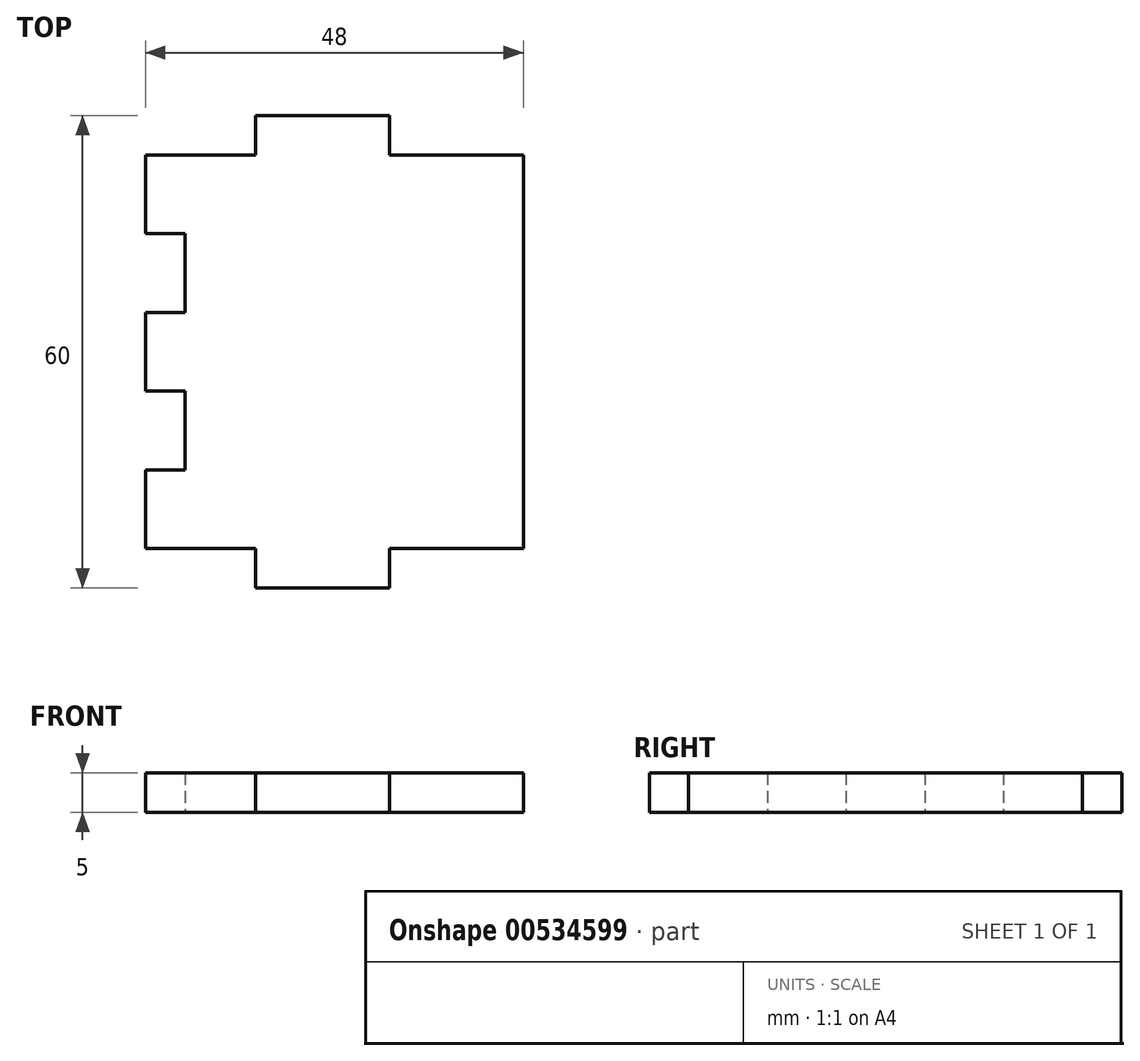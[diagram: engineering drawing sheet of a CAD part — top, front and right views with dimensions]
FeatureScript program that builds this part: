
annotation { "Feature Type Name" : "Feature", "Feature Type Description" : "" }
export const myFeature = defineFeature(function(context is Context, id is Id, definition is map)
    precondition{}
    {
        {
            var Q0;
            Q0=qCreatedBy(makeId("Top.planeOp"),FACE);
            var sketch = newSketch(context, id + "F0", { "sketchPlane" : qUnion([Q0])});
            skLineSegment(sketch, "E0.bottom", {"start": v(21.5, 25) * mm, "end": v(4.5, 25) * mm});
            skLineSegment(sketch, "E0.top", {"start": v(21.5, -25) * mm, "end": v(4.5, -25) * mm});
            skLineSegment(sketch, "E0.left", {"start": v(21.5, 25) * mm, "end": v(21.5, -25) * mm});
            skLineSegment(sketch, "E0.right", {"start": v(-21.5, 15) * mm, "end": v(-21.5, 5) * mm});
            skPoint(sketch, "E0.middle", {"position": v(0, 0) * mm});
            skLineSegment(sketch, "E1", {"start": v(21.5, -25) * mm, "end": v(21.5, -30) * mm, "construction": true});
            skLineSegment(sketch, "E2", {"start": v(21.5, -30) * mm, "end": v(-26.5, -30) * mm, "construction": true});
            skLineSegment(sketch, "E3", {"start": v(-26.5, -30) * mm, "end": v(-26.5, 30) * mm, "construction": true});
            skLineSegment(sketch, "E4", {"start": v(-26.5, 30) * mm, "end": v(21.5, 30) * mm, "construction": true});
            skLineSegment(sketch, "E5", {"start": v(21.5, 30) * mm, "end": v(21.5, 25) * mm, "construction": true});
            skLineSegment(sketch, "E6.top", {"start": v(4.5, 30) * mm, "end": v(-12.5, 30) * mm});
            skLineSegment(sketch, "E6.left", {"start": v(4.5, 25) * mm, "end": v(4.5, 30) * mm});
            skLineSegment(sketch, "E6.right", {"start": v(-12.5, 25) * mm, "end": v(-12.5, 30) * mm});
            skLineSegment(sketch, "E7.top", {"start": v(4.5, -30) * mm, "end": v(-12.5, -30) * mm});
            skLineSegment(sketch, "E7.left", {"start": v(4.5, -25) * mm, "end": v(4.5, -30) * mm});
            skLineSegment(sketch, "E7.right", {"start": v(-12.5, -25) * mm, "end": v(-12.5, -30) * mm});
            skLineSegment(sketch, "E8.trimOffspring", {"start": v(-12.5, 25) * mm, "end": v(-21.5, 25) * mm});
            skLineSegment(sketch, "E9.trimOffspring", {"start": v(-12.5, -25) * mm, "end": v(-21.5, -25) * mm});
            skLineSegment(sketch, "E10.bottom", {"start": v(-21.5, 25) * mm, "end": v(-26.5, 25) * mm});
            skLineSegment(sketch, "E10.top", {"start": v(-21.5, 15) * mm, "end": v(-26.5, 15) * mm});
            skLineSegment(sketch, "E10.right", {"start": v(-26.5, 25) * mm, "end": v(-26.5, 15) * mm});
            skLineSegment(sketch, "E11.bottom", {"start": v(-21.5, 5) * mm, "end": v(-26.5, 5) * mm});
            skLineSegment(sketch, "E11.top", {"start": v(-21.5, -5) * mm, "end": v(-26.5, -5) * mm});
            skLineSegment(sketch, "E11.right", {"start": v(-26.5, 5) * mm, "end": v(-26.5, -5) * mm});
            skLineSegment(sketch, "E12.bottom", {"start": v(-21.5, -25) * mm, "end": v(-26.5, -25) * mm});
            skLineSegment(sketch, "E12.top", {"start": v(-21.5, -15) * mm, "end": v(-26.5, -15) * mm});
            skLineSegment(sketch, "E12.right", {"start": v(-26.5, -25) * mm, "end": v(-26.5, -15) * mm});
            skLineSegment(sketch, "E13.trimOffspring", {"start": v(-21.5, -5) * mm, "end": v(-21.5, -15) * mm});
            skSolve(sketch);
        }
        {
            var Q0;
            Q0 = qSketchRegion(id + "F0", true);
            extrude(context, id + "F1", {"entities" : qUnion([Q0]), "depth" : 5 * mm, "offsetDistance" : 25 * mm});
        }
    });
